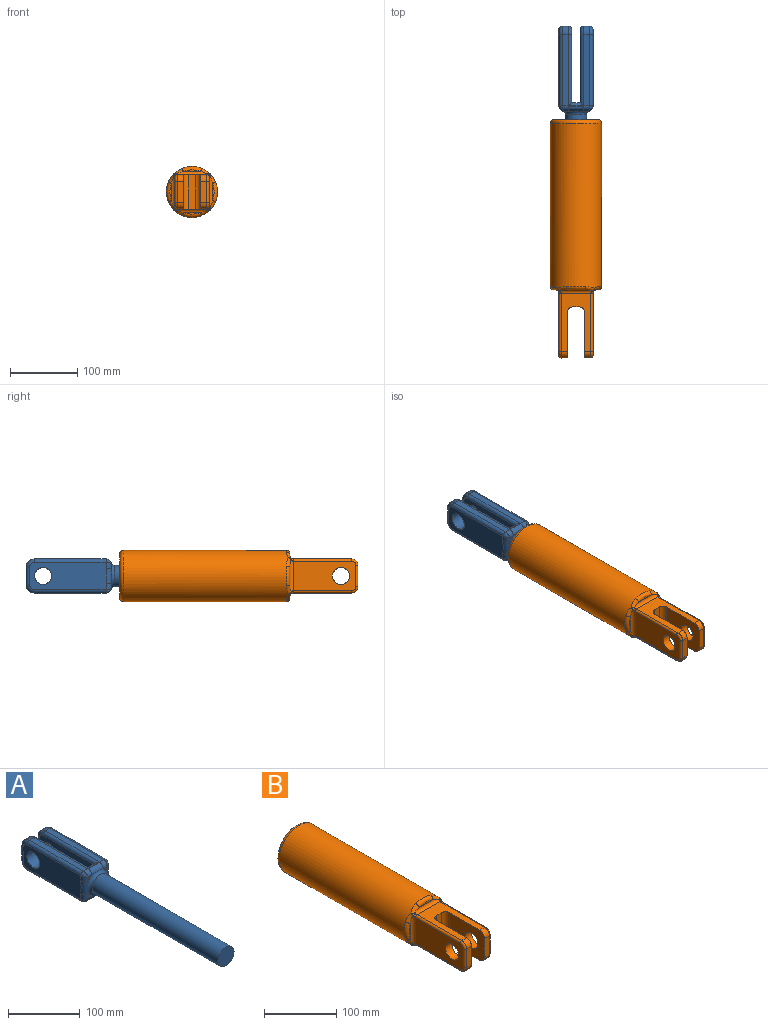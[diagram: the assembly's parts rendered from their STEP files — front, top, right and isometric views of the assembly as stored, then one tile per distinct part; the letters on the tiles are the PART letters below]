
ASSEMBLY  parts=2 mates=1
PART A: 64 faces, bbox 53.2x382x53.2 mm
  f0: plane 109.22x40.64mm, normal (1,0,0), area 3907.1mm2, adj f18,f19,f20,f22,f33,f55,f60
  f1: plane 114.71x40.64mm, normal (-1,0,0), area 4118.2mm2, adj f30,f31,f32,f33,f46,f48,f50,f57
  f2: plane 114.71x40.64mm, normal (1,0,0), area 4118.2mm2, adj f27,f28,f29,f34,f37,f39,f41,f52
  f3: plane 109.22x40.64mm, normal (-1,0,0), area 3907.1mm2, adj f18,f23,f25,f26,f34,f54,f61
  f4: plane 106.68x8.89mm, normal (0,0,-1), area 948.4mm2, adj f26,f27,f38,f53
  f5: plane 22.19x0.41mm, normal (0,0,-1), area 4.6mm2, adj f24,f40
  f6: plane 106.68x8.89mm, normal (0,0,1), area 948.4mm2, adj f19,f32,f49,f59
  f7: plane 22.19x0.41mm, normal (0,0,1), area 4.6mm2, adj f21,f47
  f8: plane 6.69x6.69mm, normal (0,-1,0), area 19mm2, adj f35,f41,f45
  f9: plane 6.69x6.69mm, normal (0,-1,0), area 19mm2, adj f35,f49,f50
  f10: plane 6.69x6.69mm, normal (0,-1,0), area 19mm2, adj f35,f42,f46
  f11: plane 25.4x8.89mm, normal (0,1,0), area 225.8mm2, adj f25,f28,f53,f62
  f12: cylinder r=15.88mm len=248.92mm, axis (0,1,0), area 24828.7mm2, adj f13,f35
  f13: plane 31.75x31.75mm, normal (0,-1,0), area 791.7mm2, adj f12
  f14: plane 25.4x8.89mm, normal (0,1,0), area 225.8mm2, adj f20,f31,f56,f59
  f15: plane 106.68x8.89mm, normal (0,0,1), area 948.4mm2, adj f23,f29,f45,f62
  f16: plane 106.68x8.89mm, normal (0,0,-1), area 948.4mm2, adj f22,f30,f42,f56
  f17: plane 6.69x6.69mm, normal (0,-1,0), area 19mm2, adj f35,f37,f38
  f18: plane 40.64x12.7mm, normal (0,1,0), area 516.1mm2, adj f0,f3,f21,f24
  f19: cylinder r=5.08mm len=106.68mm, axis (0,-1,0), area 825.5mm2, adj f0,f6,f21,f60
  f20: cylinder r=5.08mm len=25.4mm, axis (0,0,1), area 202.7mm2, adj f0,f14,f55,f60
  f21: cylinder r=5.08mm len=22.86mm, axis (-1,0,0), area 130.8mm2, adj f7,f18,f19,f23,f45,f49
  f22: cylinder r=5.08mm len=106.68mm, axis (0,-1,0), area 825.5mm2, adj f0,f16,f24,f55
  f23: cylinder r=5.08mm len=106.68mm, axis (0,-1,0), area 825.5mm2, adj f3,f15,f21,f61
  f24: cylinder r=5.08mm len=22.86mm, axis (1,0,0), area 130.8mm2, adj f5,f18,f22,f26,f38,f42
  f25: cylinder r=5.08mm len=25.4mm, axis (0,0,-1), area 202.7mm2, adj f3,f11,f54,f61
  f26: cylinder r=5.08mm len=106.68mm, axis (0,-1,0), area 825.5mm2, adj f3,f4,f24,f54
  f27: cylinder r=5.08mm len=106.68mm, axis (0,1,0), area 851.3mm2, adj f2,f4,f36,f52
  f28: cylinder r=5.08mm len=25.4mm, axis (0,0,-1), area 202.7mm2, adj f2,f11,f52,f63
  f29: cylinder r=5.08mm len=106.68mm, axis (0,1,0), area 851.3mm2, adj f2,f15,f43,f63
  f30: cylinder r=5.08mm len=106.68mm, axis (0,-1,0), area 851.3mm2, adj f1,f16,f44,f57
  f31: cylinder r=5.08mm len=25.4mm, axis (0,0,1), area 202.7mm2, adj f1,f14,f57,f58
  f32: cylinder r=5.08mm len=106.68mm, axis (0,-1,0), area 851.3mm2, adj f1,f6,f51,f58
  f33: cylinder r=12.7mm len=25.4mm, axis (1,0,0), area 1520.1mm2, adj f0,f1
  f34: cylinder r=12.7mm len=25.4mm, axis (1,0,0), area 1520.1mm2, adj f2,f3
  f35: torus R=20.96mm, axis (0,-1,0), area 808.6mm2, adj f8,f9,f10,f12,f17,f39,f40,f47
  f36: bspline ~8.04x7.62mm, area 62.9mm2, adj f27,f37,f38
  f37: cylinder r=7.62mm len=9.23mm, axis (0,0,1), area 99.4mm2, adj f2,f17,f36,f39
  f38: cylinder r=7.62mm len=9.23mm, axis (1,0,0), area 99.4mm2, adj f4,f17,f24,f36,f40
  f39: bspline ~27.44x8.4mm, area 237.6mm2, adj f2,f35,f37,f41
  f40: bspline ~27.44x8.4mm, area 237.6mm2, adj f5,f35,f38,f42
  f41: cylinder r=7.62mm len=9.23mm, axis (0,0,1), area 99.4mm2, adj f2,f8,f39,f43
  f42: cylinder r=7.62mm len=9.23mm, axis (1,0,0), area 99.4mm2, adj f10,f16,f24,f40,f44
  f43: bspline ~8.04x7.62mm, area 62.9mm2, adj f29,f41,f45
  f44: bspline ~8.04x7.62mm, area 62.9mm2, adj f30,f42,f46
  f45: cylinder r=7.62mm len=9.23mm, axis (-1,0,0), area 99.4mm2, adj f8,f15,f21,f43,f47
  f46: cylinder r=7.62mm len=9.23mm, axis (0,0,-1), area 99.4mm2, adj f1,f10,f44,f48
  f47: bspline ~27.44x8.4mm, area 237.6mm2, adj f7,f35,f45,f49
  f48: bspline ~27.44x8.4mm, area 237.6mm2, adj f1,f35,f46,f50
  f49: cylinder r=7.62mm len=9.23mm, axis (-1,0,0), area 99.4mm2, adj f6,f9,f21,f47,f51
  f50: cylinder r=7.62mm len=9.23mm, axis (0,0,-1), area 99.4mm2, adj f1,f9,f48,f51
  f51: bspline ~8.04x7.62mm, area 62.9mm2, adj f32,f49,f50
  f52: torus R=7.62mm, axis (1,0,0), area 136mm2, adj f2,f27,f28,f53
  f53: cylinder r=12.7mm len=12.7mm, axis (-1,0,0), area 177.3mm2, adj f4,f11,f52,f54
  f54: torus R=7.62mm, axis (-1,0,0), area 136mm2, adj f3,f25,f26,f53
  f55: torus R=7.62mm, axis (1,0,0), area 136mm2, adj f0,f20,f22,f56
  f56: cylinder r=12.7mm len=12.7mm, axis (-1,0,0), area 177.3mm2, adj f14,f16,f55,f57
  f57: torus R=7.62mm, axis (1,0,0), area 136mm2, adj f1,f30,f31,f56
  f58: torus R=7.62mm, axis (1,0,0), area 136mm2, adj f1,f31,f32,f59
  f59: cylinder r=12.7mm len=12.7mm, axis (1,0,0), area 177.3mm2, adj f6,f14,f58,f60
  f60: torus R=7.62mm, axis (1,0,0), area 136mm2, adj f0,f19,f20,f59
  f61: torus R=7.62mm, axis (-1,0,0), area 136mm2, adj f3,f23,f25,f62
  f62: cylinder r=12.7mm len=12.7mm, axis (1,0,0), area 177.3mm2, adj f11,f15,f61,f63
  f63: torus R=7.62mm, axis (1,0,0), area 136mm2, adj f2,f28,f29,f62
PART B: 60 faces, bbox 82.5x356.4x82.5 mm
  f0: plane 25.4x2.54mm, normal (0,-1,0), area 43.4mm2, adj f28,f46
  f1: plane 25.4x2.54mm, normal (0,-1,0), area 43.4mm2, adj f25,f55
  f2: plane 25.4x2.54mm, normal (0,-1,0), area 43.4mm2, adj f27,f54
  f3: plane 68.28x50.8mm, normal (-1,0,0), area 2922mm2, adj f4,f11,f12,f13,f15,f17,f19
  f4: plane 31.5x9.53mm, normal (0,-1,0), area 300mm2, adj f3,f17,f19,f39
  f5: plane 93.35x44.45mm, normal (1,0,0), area 3624.5mm2, adj f15,f28,f37,f38,f39,f40,f41
  f6: plane 93.35x44.45mm, normal (-1,0,0), area 3624.5mm2, adj f14,f25,f30,f31,f32,f33,f34
  f7: plane 31.5x9.53mm, normal (0,-1,0), area 300mm2, adj f8,f16,f18,f32
  f8: plane 68.28x50.8mm, normal (1,0,0), area 2922mm2, adj f7,f9,f12,f13,f14,f16,f18
  f9: cylinder r=7.92mm len=50.8mm, axis (0,0,-1), area 631.9mm2, adj f8,f10,f12,f13
  f10: plane 50.8x9.56mm, normal (0,-1,0), area 485.7mm2, adj f9,f11,f12,f13
  f11: cylinder r=7.92mm len=50.8mm, axis (0,0,-1), area 631.9mm2, adj f3,f10,f12,f13
  f12: plane 86.87x44.45mm, normal (0,0,1), area 2197.9mm2, adj f3,f8,f9,f10,f11,f18,f19,f26
  f13: plane 86.87x44.45mm, normal (0,0,-1), area 2197.9mm2, adj f3,f8,f9,f10,f11,f16,f17,f27
  f14: cylinder r=12.7mm len=25.4mm, axis (1,0,0), area 1013.4mm2, adj f6,f8
  f15: cylinder r=12.7mm len=25.4mm, axis (1,0,0), area 1013.4mm2, adj f3,f5
  f16: cylinder r=9.65mm len=9.65mm, axis (1,0,0), area 144.4mm2, adj f7,f8,f13,f33
  f17: cylinder r=9.65mm len=9.65mm, axis (1,0,0), area 144.4mm2, adj f3,f4,f13,f40
  f18: cylinder r=9.65mm len=9.65mm, axis (-1,0,0), area 144.4mm2, adj f7,f8,f12,f31
  f19: cylinder r=9.65mm len=9.65mm, axis (-1,0,0), area 144.4mm2, adj f3,f4,f12,f38
  f20: cylinder r=38.1mm len=246.76mm, axis (0,-1,0), area 58546.7mm2, adj f44,f45,f46,f47,f48,f49,f52,f53
  f21: plane 66.04x66.04mm, normal (0,1,0), area 2633.6mm2, adj f23,f59
  f22: plane 25.4x2.54mm, normal (0,-1,0), area 43.4mm2, adj f26,f47
  f23: cylinder r=15.88mm len=203.2mm, axis (0,1,0), area 20268.3mm2, adj f21,f24
  f24: plane 31.75x31.75mm, normal (0,1,0), area 791.7mm2, adj f23
  f25: cylinder r=5.08mm len=48.15mm, axis (0,0,1), area 326.5mm2, adj f1,f6,f29,f35,f53,f57
  f26: cylinder r=5.08mm len=48.15mm, axis (1,0,0), area 326.5mm2, adj f12,f22,f29,f36,f45,f49
  f27: cylinder r=5.08mm len=48.15mm, axis (-1,0,0), area 326.5mm2, adj f2,f13,f35,f42,f52,f56
  f28: cylinder r=5.08mm len=48.15mm, axis (0,0,1), area 326.5mm2, adj f0,f5,f36,f42,f44,f48
  f29: bspline ~4.43x4.43mm, area 15.8mm2, adj f25,f26,f30,f51
  f30: cylinder r=3.17mm len=86.87mm, axis (0,1,0), area 433.2mm2, adj f6,f12,f29,f31
  f31: torus R=6.48mm, axis (1,0,0), area 66.6mm2, adj f6,f18,f30,f32
  f32: cylinder r=3.17mm len=31.5mm, axis (0,0,-1), area 157.1mm2, adj f6,f7,f31,f33
  f33: torus R=6.48mm, axis (1,0,0), area 66.6mm2, adj f6,f16,f32,f34
  f34: cylinder r=3.17mm len=86.87mm, axis (0,-1,0), area 433.2mm2, adj f6,f13,f33,f35
  f35: bspline ~4.43x4.43mm, area 15.8mm2, adj f25,f27,f34,f58
  f36: bspline ~4.43x4.43mm, area 15.8mm2, adj f26,f28,f37,f43
  f37: cylinder r=3.17mm len=86.87mm, axis (0,-1,0), area 433.2mm2, adj f5,f12,f36,f38
  f38: torus R=6.48mm, axis (-1,0,0), area 66.6mm2, adj f5,f19,f37,f39
  f39: cylinder r=3.17mm len=31.5mm, axis (0,0,-1), area 157.1mm2, adj f4,f5,f38,f40
  f40: torus R=6.48mm, axis (-1,0,0), area 66.6mm2, adj f5,f17,f39,f41
  f41: cylinder r=3.17mm len=86.87mm, axis (0,1,0), area 433.2mm2, adj f5,f13,f40,f42
  f42: bspline ~4.43x4.43mm, area 15.8mm2, adj f27,f28,f41,f50
  f43: bspline ~5.75x3.83mm, area 6.3mm2, adj f36,f44,f45
  f44: bspline ~18.58x10.69mm, area 90.8mm2, adj f20,f28,f43,f46
  f45: bspline ~18.58x10.69mm, area 90.8mm2, adj f20,f26,f43,f47
  f46: torus R=33.02mm, axis (0,1,0), area 228.4mm2, adj f0,f20,f44,f48
  f47: torus R=33.02mm, axis (0,1,0), area 228.4mm2, adj f20,f22,f45,f49
  f48: bspline ~18.58x10.69mm, area 90.8mm2, adj f20,f28,f46,f50
  f49: bspline ~18.58x10.69mm, area 90.8mm2, adj f20,f26,f47,f51
  f50: bspline ~5.75x3.83mm, area 6.3mm2, adj f42,f48,f52
  f51: bspline ~5.75x3.83mm, area 6.3mm2, adj f29,f49,f53
  f52: bspline ~18.58x10.69mm, area 90.8mm2, adj f20,f27,f50,f54
  f53: bspline ~18.58x10.69mm, area 90.8mm2, adj f20,f25,f51,f55
  f54: torus R=33.02mm, axis (0,1,0), area 228.4mm2, adj f2,f20,f52,f56
  f55: torus R=33.02mm, axis (0,1,0), area 228.4mm2, adj f1,f20,f53,f57
  f56: bspline ~18.58x10.69mm, area 90.8mm2, adj f20,f27,f54,f58
  f57: bspline ~18.58x10.69mm, area 90.8mm2, adj f20,f25,f55,f58
  f58: bspline ~5.75x3.83mm, area 6.3mm2, adj f35,f56,f57
  f59: torus R=33.02mm, axis (0,1,0), area 1817.7mm2, adj f20,f21
PLACE A t=(-119.48,382.2,112.85)mm
PLACE B t=(-14.45,71.07,122.15)mm fixed
MATE slider A.f12 <-> B.f20  axis (0,-1,0) through (-54.67,128.2,147.55)mm
